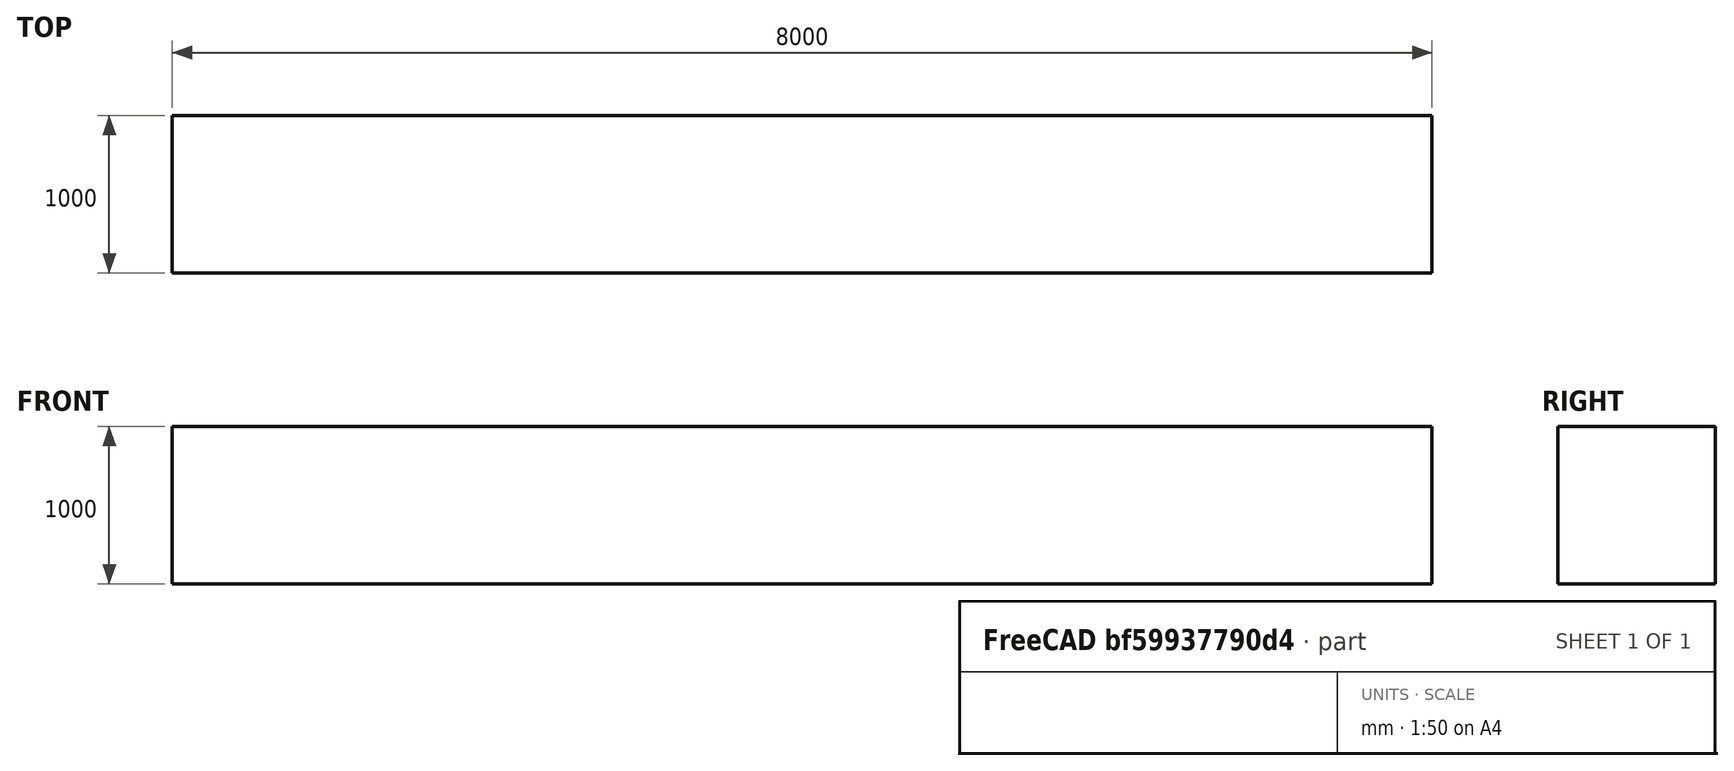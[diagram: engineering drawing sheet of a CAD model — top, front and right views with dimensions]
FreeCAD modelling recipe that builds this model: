
FCSTD DOCUMENT  (FreeCAD 0.17R13245 (Git))
Label: FemCalculixCantilever3D_newSolver
License: CC-BY 3.0
LicenseURL: http://creativecommons.org/licenses/by/3.0/
objects: Fem::FemSolverObjectPython×3, Fem::FemMeshObjectPython×3, Fem::FemResultObjectPython×2, Part::Box×1, Fem::ConstraintFixed×1, Fem::ConstraintForce×1, App::FeaturePython×1, App::MaterialObjectPython×1, Fem::FemPostPipeline×1, Fem::FemAnalysis×1
note: 1 computed .brp shape members not serialized (recipe doc carries the construction recipe); baked Part::Feature solids carry a one-line shape summary decoded from their .brp

FEATURE [Part::Box] Box  label="Cube"
  AttacherType = Attacher::AttachEngine3D
  Height = 1000
  Length = 8000
  Width = 1000
FEATURE [Fem::ConstraintFixed] FemConstraintFixed
  NormalDirection = (-1,0,0)
  Normals = (16) [(-1,0,0),(-1,0,0),(-1,0,0),(-1,0,0),(-1,0,0),(-1,0,0),(-1,0,0),(-1,0,0),(-1,0,0),(-1,0,0),(-1,0,0),(-1,0,0),(-1,0,0),(-1,0,0),(-1,0,0),(-1,0,0)]
  Points = (16) [(0,1000,0),(0,1000,333.333),(0,1000,666.667),(0,1000,1000),(0,666.667,0),(0,666.667,333.333),(0,666.667,666.667),(0,666.667,1000),(0,333.333,0),+7 more]
  References = -> [Box]
  Scale = 33
FEATURE [Fem::ConstraintForce] FemConstraintForce
  Direction = -> Box [Edge7]
  DirectionVector = (0,0,-1)
  Force = 9000000
  NormalDirection = (1,0,0)
  Points = (16) [(8000,1000,0),(8000,1000,333.333),(8000,1000,666.667),(8000,1000,1000),(8000,666.667,0),(8000,666.667,333.333),(8000,666.667,666.667),+9 more]
  References = -> [Box]
  Reversed = true
  Scale = 33
FEATURE [Fem::FemSolverObjectPython] SolverCalculiX  # FEM object (typed FeaturePython)
  AnalysisType = 0
  BeamShellResultOutput3D = false
  EigenmodeHighLimit = 0
  EigenmodeLowLimit = 0
  EigenmodesCount = 15
  GeometricalNonlinearity = 0
  IterationsControlParameterCutb = 0.25,0.5,0.75,0.85,,,1.5,
  IterationsControlParameterIter = 4,8,9,200,10,400,,200,,
  IterationsControlParameterTimeUse = false
  IterationsThermoMechMaximum = 2000
  IterationsUserDefinedIncrementations = false
  IterationsUserDefinedTimeStepLength = false
  MaterialNonlinearity = 0
  MatrixSolverType = 0
  SplitInputWriter = false
  ThermoMechSteadyState = true
  TimeEnd = 1
  TimeInitialStep = 1
FEATURE [Fem::FemSolverObjectPython] SolverZ88  # FEM object (typed FeaturePython)
  AnalysisType = 0
FEATURE [App::FeaturePython] Elasticity  # WARN: FeaturePython — macro-defined, semantics opaque (R4)
  BiCGstablDegree = 0
  Bubbles = false
  CalculatePangle = false
  CalculatePrincipal = false
  CalculateStrains = false
  CalculateStresses = false
  DoFrequencyAnalysis = false
  EigenmodesCount = 5
  LinearDirectMethod = 0
  LinearIterations = 500
  LinearIterativeMethod = 2
  LinearPreconditioning = 2
  LinearSolverType = 1
  LinearTolerance = 1e-08
  Priority = 10
  Stabilize = true
  SteadyStateTolerance = 1e-05
FEATURE [App::MaterialObjectPython] SolidMaterial  # material (typed FeaturePython)
  Category = 0
  Material = Density=7900.0 kg/m^3,Description=Standard steel material for CalculiX sample calculations,Father=Metal,Name=CalculiX-Steel,PoissonRatio=0.3,+4 more (map truncated)
FEATURE [Fem::FemMeshObjectPython] FEMMeshGmsh  # FEM object (typed FeaturePython)
  Algorithm2D = 0
  Algorithm3D = 0
  CharacteristicLengthMax = 0
  CharacteristicLengthMin = 0
  CoherenceMesh = true
  ElementDimension = 0
  ElementOrder = 1
  GeometryTolerance = 1e-06
  GroupsOfNodes = false
  HighOrderOptimize = false
  OptimizeNetgen = false
  OptimizeStd = true
  Part = -> Box
  RecombineAll = false
FEATURE [Fem::FemMeshObjectPython] Result_mesh  # FEM object (typed FeaturePython)
FEATURE [Fem::FemResultObjectPython] CalculiX_static_results  # FEM object (typed FeaturePython)
  DisplacementLengths = [0,0,0,0,87.937,87.9368,87.938,87.9383,0,0,0,0,0,0,0,0,0,0,0,0,87.5423,87.6436,87.6436,87.943,87.9418,87.9423,87.5435,87.6449,87.6448,87.9437,87.9421,87.9428,1.98318,5.68761,11.3939,18.906,28.0027,38.4037,49.8592,62.1074,74.8816,0.880806,+478 more]
  DisplacementVectors = (520) [(0,0,0),(0,0,0),(0,0,0),(0,0,0),(8.16317,0.00342817,-87.5573),(-8.1624,-0.00296136,-87.5572),(8.16362,-0.0026403,-87.5583),+513 more]
  Eigenmode = 0
  EigenmodeFrequency = 0
  MaxShear = [172.603,172.608,172.648,172.652,4.52873,4.65036,4.54311,4.76657,41.5712,94.9532,94.9677,162.938,163.553,163.576,41.5961,94.9812,94.9935,162.941,163.577,163.601,14.4287,9.18759,9.18418,6.23008,4.98529,5.02115,14.352,9.11854,9.13007,6.21069,+490 more]
  Mesh = -> Result_mesh
  NodeNumbers = [1,2,3,4,5,6,7,8,9,10,11,12,13,14,15,16,17,18,19,20,21,22,23,24,25,26,27,28,29,30,31,32,33,34,35,36,37,38,39,40,41,42,43,44,45,46,47,48,49,50,51,52,53,54,55,56,57,58,59,60,61,62,63,64,65,66,67,68,69,+451 more]
  PrincipalMax = [470.431,-125.244,470.551,-125.283,4.77203,4.28426,4.93769,4.20394,41.5632,-70.2968,260.214,447.341,462.902,462.988,41.5909,-70.3086,260.285,-121.472,-135.828,-135.873,14.2786,12.1108,6.10831,3.86866,4.22195,4.27473,14.3541,12.1047,6.14313,+491 more]
  PrincipalMed = [146.956,-147.001,147.02,-147.049,1.31953,-1.00288,1.44829,-1.04617,-0.0187173,-138.678,138.685,261.972,256.839,256.881,-0.0121327,-138.733,138.734,-261.976,-256.881,-256.924,-0.0684757,-2.59888,2.39176,-0.0747865,0.49117,0.447097,0.0119465,+493 more]
  PrincipalMin = [125.224,-470.46,125.256,-470.587,-4.28544,-5.01647,-4.14854,-5.3292,-41.5792,-260.203,70.2781,121.464,135.796,135.836,-41.6013,-260.271,70.2983,-447.355,-462.982,-463.075,-14.5789,-6.26436,-12.26,-8.59149,-5.74864,-5.76757,-14.3499,+493 more]
  ResultType = Fem::FemResultMechanical
  Stats = [-8.16894,-6.16628e-06,8.16895,-0.266968,-2.61048e-05,0.266841,-87.5635,-34.8376,0,0,35.1365,87.9437,2.27927,136.634,438.103,-135.873,71.1596,470.551,-261.976,0.0027446,261.972,-470.587,-71.2347,135.836,1.31591,71.1971,227.385,0,0,0,0,0,0,0,+5 more]
  StrainVectors = (520) [(0.00178534,-0.000111636,-0.000259206),(-0.00178542,0.000111593,0.000259149),(0.0017858,-0.000111609,-0.000259287),+517 more]
  StressValues = [334.87,334.868,334.944,334.951,7.91748,8.0798,7.93914,8.27009,72.0034,166.596,166.62,283.107,286.454,286.496,72.0466,166.642,166.663,283.113,286.497,286.542,24.9914,16.8443,16.8209,11.0304,8.72544,8.7784,24.8584,16.7689,16.7557,11.1209,+490 more]
  StressVectors = (520) [(459.773,153.338,129.5),(-459.807,-153.367,-129.531),(459.898,153.392,129.537),(-459.936,-153.415,-129.568),(4.54783,-0.158025,-2.58368),+515 more]
  Time = 0
FEATURE [Fem::FemMeshObjectPython] Result_mesh001  # FEM object (typed FeaturePython)
FEATURE [Fem::FemResultObjectPython] Z88_static_results  # FEM object (typed FeaturePython)
  DisplacementLengths = [0,0,0,0,87.937,87.9368,87.9381,87.9383,0,0,0,0,0,0,0,0,0,0,0,0,87.5423,87.6436,87.6437,87.943,87.9418,87.9423,87.5435,87.6449,87.6448,87.9437,87.9421,87.9428,1.98319,5.68761,11.3939,18.906,28.0027,38.4036,49.8592,62.1075,74.8816,0.880806,+478 more]
  DisplacementVectors = (520) [(0,0,0),(0,0,0),(0,0,0),(0,0,0),(8.16317,0.00342817,-87.5573),(-8.1624,-0.00296136,-87.5572),(8.16362,-0.0026403,-87.5583),+513 more]
  Eigenmode = 0
  EigenmodeFrequency = 0
  Mesh = -> Result_mesh001
  NodeNumbers = [1,2,3,4,5,6,7,8,9,10,11,12,13,14,15,16,17,18,19,20,21,22,23,24,25,26,27,28,29,30,31,32,33,34,35,36,37,38,39,40,41,42,43,44,45,46,47,48,49,50,51,52,53,54,55,56,57,58,59,60,61,62,63,64,65,66,67,68,69,+451 more]
  ResultType = Fem::FemResultMechanical
  Stats = [-8.16894,-6.21235e-06,8.16895,-0.266968,-2.61114e-05,0.266841,-87.5635,-34.8376,0,0,35.1365,87.9437,0,0,0,0,0,0,0,0,0,0,0,0,0,0,0,0,0,0,0,0,0,0,0,0,0,0,0]
  Time = 0
FEATURE [Fem::FemPostPipeline] SolverElmerResult
  Mode = 0
FEATURE [Fem::FemSolverObjectPython] SolverElmer  # FEM object (typed FeaturePython)
  ElmerResult = -> SolverElmerResult
  Group = -> [Elasticity]
  SteadyStateMaxIterations = 1
  SteadyStateMinIterations = 0
FEATURE [Fem::FemAnalysis] Analysis
  Group = -> [SolverCalculiX,SolverZ88,SolverElmer,SolidMaterial,FemConstraintFixed,FemConstraintForce,FEMMeshGmsh,CalculiX_static_results,Z88_static_results,SolverElmerResult]
